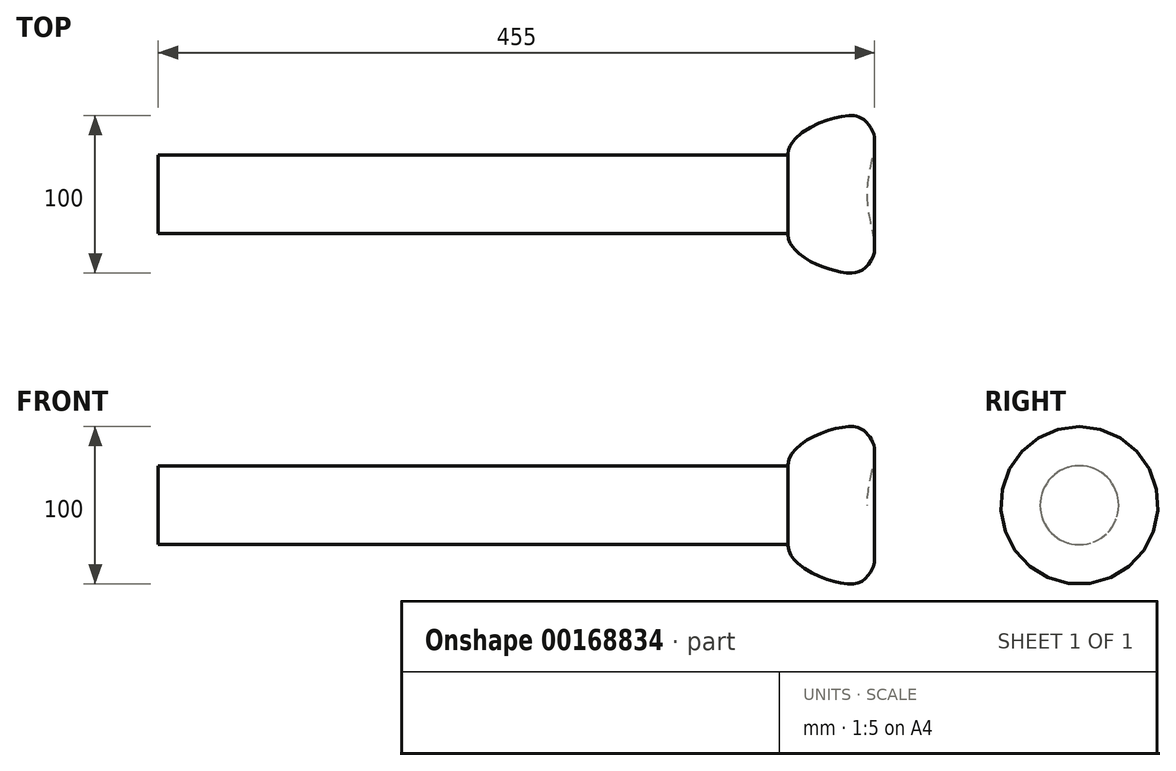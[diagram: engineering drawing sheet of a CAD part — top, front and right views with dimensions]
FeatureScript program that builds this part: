
annotation { "Feature Type Name" : "Feature", "Feature Type Description" : "" }
export const myFeature = defineFeature(function(context is Context, id is Id, definition is map)
    precondition{}
    {
        {
            assignVariable(context, id + "F0", {"name" : "L", "anyValue" : 400 * mm});
        }
        {
            var Q0;
            Q0=qCreatedBy(makeId("Right.planeOp"),FACE);
            var sketch = newSketch(context, id + "F1", { "sketchPlane" : qUnion([Q0])});
            skCircle(sketch, "E0", {"center": v(0, 0) * mm, "radius": 25 * mm});
            skSolve(sketch);
        }
        {
            var Q0;
            Q0 = qSketchRegion(id + "F1", true);
            extrude(context, id + "F2", {"entities" : qUnion([Q0]), "endBound" : BoundingType.SYMMETRIC, "depth" : getVariable(context, 'L')});
        }
        {
            var Q0;
            Q0=qCreatedBy(makeId("Front.planeOp"),FACE);
            var sketch = newSketch(context, id + "F3", { "sketchPlane" : qUnion([Q0])});
            skLineSegment(sketch, "E1.0", {"start": v(200, 25) * mm, "end": v(200, -25) * mm});
            skLineSegment(sketch, "E2", {"start": v(200, 0) * mm, "end": v(250, 0) * mm});
            skLineSegment(sketch, "E3", {"start": v(250, 0) * mm, "end": v(250, -17.4) * mm, "construction": true});
            skLineSegment(sketch, "E4", {"start": v(191.91, 50) * mm, "end": v(255, 50) * mm, "construction": true});
            skLineSegment(sketch, "E5", {"start": v(255, 50) * mm, "end": v(255, 0) * mm, "construction": true});
            skFitSpline(sketch, "E6", {"points": [v(200, 25) * mm, v(239.63, 50) * mm, v(251.36, 43.93) * mm, v(255, 34.62) * mm, v(250, 0) * mm], "startDerivative": vector(-6.84, 120.83) * mm, "endDerivative": vector(0, -134.1) * mm});
            skSolve(sketch);
        }
        {
            var Q0;
            Q0 = qSketchRegion(id + "F3", true);
            var Q1;
            Q1=sQuery(id+"F3.wireOp",EDGE,"E2");
            revolve(context, id + "F4", {"operationType" : NewBodyOperationType.ADD, "entities" : qUnion([Q0]), "axis" : qUnion([Q1]), "revolveType" : RevolveType.FULL});
        }
    });
